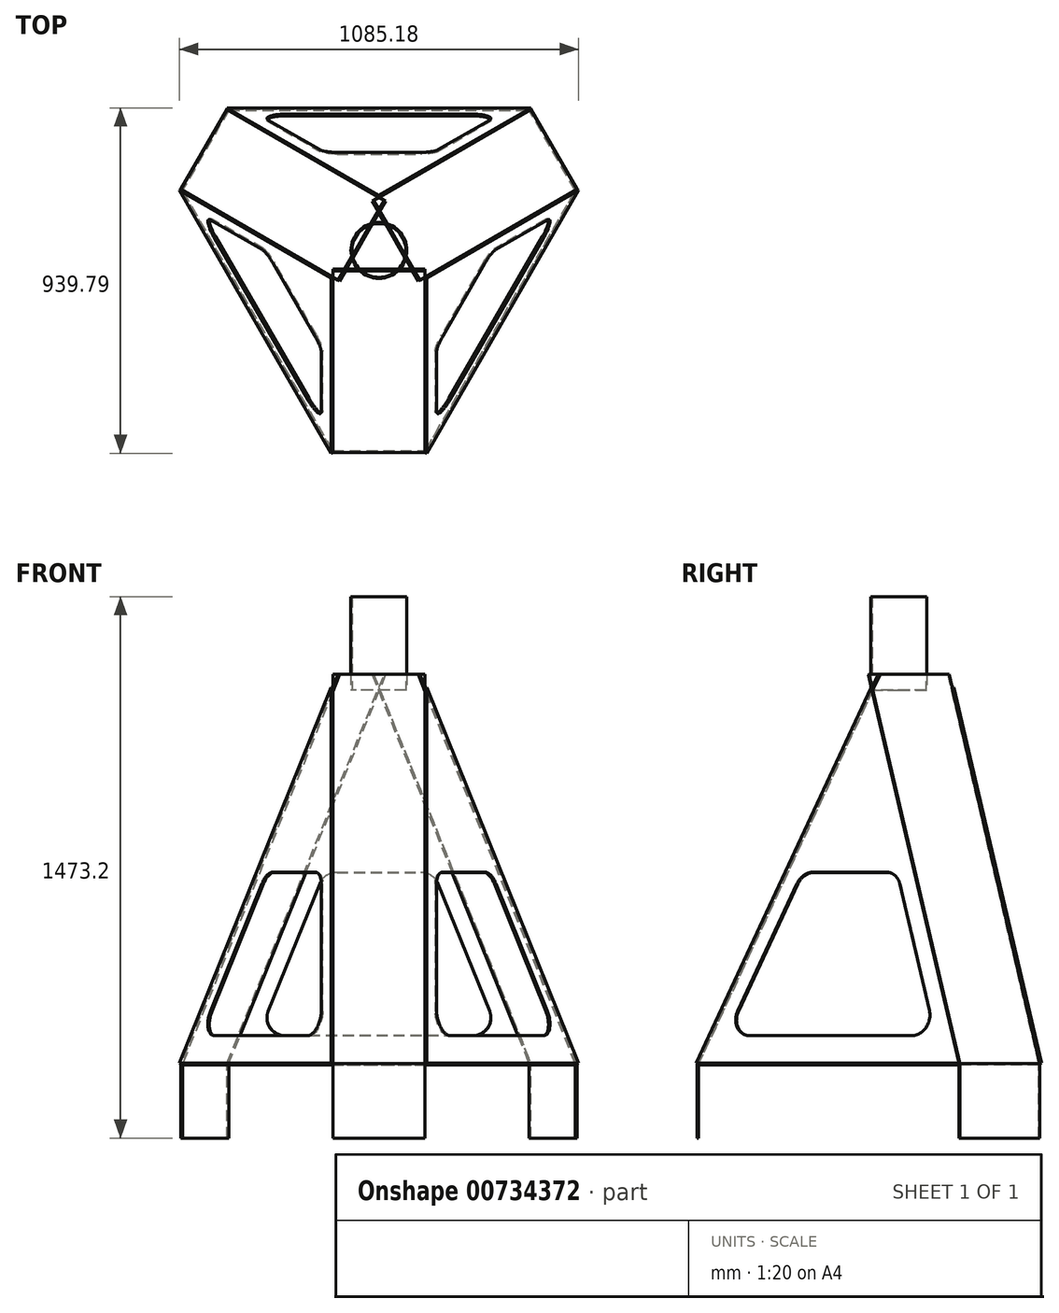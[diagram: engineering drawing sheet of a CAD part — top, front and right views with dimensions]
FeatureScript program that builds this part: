
annotation { "Feature Type Name" : "Feature", "Feature Type Description" : "" }
export const myFeature = defineFeature(function(context is Context, id is Id, definition is map)
    precondition{}
    {
        {
            var Q0;
            Q0=qCreatedBy(makeId("Top.planeOp"),FACE);
            var sketch = newSketch(context, id + "F0", { "sketchPlane" : qUnion([Q0])});
            skCircle(sketch, "E0", {"center": v(0, 0) * mm, "radius": 558.8 * mm});
            skLineSegment(sketch, "E1", {"start": v(0, 0) * mm, "end": v(0, -189.05) * mm});
            skLineSegment(sketch, "E2", {"start": v(-125.57, -544.5) * mm, "end": v(-534.34, 163.5) * mm});
            skLineSegment(sketch, "E3.1.0", {"start": v(534.34, 163.5) * mm, "end": v(125.57, -544.5) * mm});
            skLineSegment(sketch, "E3.2.0", {"start": v(-408.77, 381) * mm, "end": v(408.77, 381) * mm});
            skLineSegment(sketch, "E4", {"start": v(-125.57, -544.5) * mm, "end": v(125.57, -544.5) * mm});
            skLineSegment(sketch, "E5", {"start": v(-408.77, 381) * mm, "end": v(-534.34, 163.5) * mm});
            skLineSegment(sketch, "E6", {"start": v(408.77, 381) * mm, "end": v(534.34, 163.5) * mm});
            skSolve(sketch);
        }
        {
            var Q0;
            {var subQ0=sQuery(id+"F0.wireOp",EDGE,"E2");Q0=makeQuery(id+"F0.imprint","IMPRINT",FACE,{"disambiguationData":[TD([[makeQuery(id+"F0.imprint","IMPRINT",EDGE,{"derivedFrom":subQ0}),-1.0]])]});}
            extrude(context, id + "F1", {"entities" : qUnion([Q0]), "depth" : 4.83 * mm, "offsetDistance" : 25.4 * mm});
        }
        {
            var Q0;
            Q0=makeQuery(id+"F1.opExtrude","CAP_FACE",FACE,{"disambiguationData":[OSD([sQuery(id+"F0.wireOp",EDGE,"E2"),sQuery(id+"F0.wireOp",EDGE,"E3.1.0"),sQuery(id+"F0.wireOp",EDGE,"E3.2.0"),sQuery(id+"F0.wireOp",EDGE,"E4"),sQuery(id+"F0.wireOp",EDGE,"E5"),sQuery(id+"F0.wireOp",EDGE,"E6")])],"isStart":false});
            var sketch = newSketch(context, id + "F2", { "sketchPlane" : qUnion([Q0])});
            skLineSegment(sketch, "E7.bottom", {"start": v(-125.57, -544.5) * mm, "end": v(125.57, -544.5) * mm});
            skLineSegment(sketch, "E7.top", {"start": v(-125.57, -549.33) * mm, "end": v(125.57, -549.33) * mm});
            skLineSegment(sketch, "E7.left", {"start": v(-125.57, -544.5) * mm, "end": v(-125.57, -549.33) * mm});
            skLineSegment(sketch, "E7.right", {"start": v(125.57, -544.5) * mm, "end": v(125.57, -549.33) * mm});
            skSolve(sketch);
        }
        {
            var Q0;
            Q0 = qSketchRegion(id + "F2", true);
            extrude(context, id + "F3", {"entities" : qUnion([Q0]), "oppositeDirection" : true, "depth" : 203.2 * mm, "offsetDistance" : 25.4 * mm});
        }
        {
            var Q0;
            Q0=makeQuery(id+"F3.opExtrude","SWEPT_BODY",BODY,{"disambiguationData":[OSD([sQuery(id+"F2.wireOp",EDGE,"E7.bottom"),sQuery(id+"F2.wireOp",EDGE,"E7.top"),sQuery(id+"F2.wireOp",EDGE,"E7.left"),sQuery(id+"F2.wireOp",EDGE,"E7.right")])]});
            var Q1;
            Q1=sQuery(id+"F0.wireOp",EDGE,"E0");
            circularPattern(context, id + "F4", {"entities" : qUnion([Q0]), "axis" : qUnion([Q1]), "angle" : 360 * degree, "instanceCount" : 3, "equalSpace" : true});
        }
        {
            var Q0;
            Q0=makeQuery(id+"F1.opExtrude","CAP_FACE",FACE,{"disambiguationData":[OSD([sQuery(id+"F0.wireOp",EDGE,"E2"),sQuery(id+"F0.wireOp",EDGE,"E3.1.0"),sQuery(id+"F0.wireOp",EDGE,"E3.2.0"),sQuery(id+"F0.wireOp",EDGE,"E4"),sQuery(id+"F0.wireOp",EDGE,"E5"),sQuery(id+"F0.wireOp",EDGE,"E6")])],"isStart":false});
            cPlane(context, id + "F5", {"entities" : qUnion([Q0]), "cplaneType" : CPlaneType.OFFSET, "offset" : 1016 * mm, "width" : 152.4 * mm, "height" : 152.4 * mm});
        }
        {
            var Q0;
            Q0=qCreatedBy(id+"F5.planeOp",FACE);
            var sketch = newSketch(context, id + "F6", { "sketchPlane" : qUnion([Q0])});
            skPoint(sketch, "E8.middle", {"position": v(0, 0) * mm});
            skCircle(sketch, "E9", {"center": v(0, 0) * mm, "radius": 76.2 * mm});
            skCircle(sketch, "E10", {"center": v(0, 0) * mm, "radius": 73.15 * mm});
            skSolve(sketch);
        }
        {
            var Q0;
            Q0 = qSketchRegion(id + "F6", true);
            extrude(context, id + "F7", {"entities" : qUnion([Q0]), "depth" : 254 * mm, "offsetDistance" : 25.4 * mm});
        }
        {
            var Q0;
            Q0=makeQuery(id+"F4.opPattern","COPY",EDGE,{"derivedFrom":makeQuery(id+"F3.opExtrude","CAP_EDGE",EDGE,{"disambiguationData":[OSD([sQuery(id+"F2.wireOp",EDGE,"E7.top")])],"isStart":true}),"instanceName":"1"});
            cPlane(context, id + "F8", {"entities" : qUnion([Q0]), "cplaneType" : CPlaneType.LINE_ANGLE, "offset" : 25.4 * mm, "angle" : 65 * degree, "width" : 152.4 * mm, "height" : 152.4 * mm});
        }
        {
            var Q0;
            Q0=qCreatedBy(id+"F8.planeOp",FACE);
            var sketch = newSketch(context, id + "F9", { "sketchPlane" : qUnion([Q0])});
            skLineSegment(sketch, "E11.0", {"start": v(-68, -251.06) * mm, "end": v(175.98, -191.53) * mm});
            skLineSegment(sketch, "E12", {"start": v(-68, -251.06) * mm, "end": v(-344.96, 884.04) * mm});
            skLineSegment(sketch, "E13", {"start": v(-344.96, 884.04) * mm, "end": v(-100.98, 943.57) * mm});
            skLineSegment(sketch, "E14", {"start": v(-100.98, 943.57) * mm, "end": v(175.98, -191.53) * mm});
            skSolve(sketch);
        }
        {
            var Q0;
            Q0=makeQuery(id+"F9.imprint","IMPRINT",FACE,{"disambiguationData":[TD([[makeQuery(id+"F9.imprint","IMPRINT",EDGE,{"derivedFrom":sQuery(id+"F9.wireOp",EDGE,"E11.0")}),1.0]])]});
            extrude(context, id + "F10", {"entities" : qUnion([Q0]), "oppositeDirection" : true, "depth" : 4.83 * mm, "offsetDistance" : 25.4 * mm});
        }
        {
            var Q0;
            Q0=makeQuery(id+"F10.opExtrude","SWEPT_BODY",BODY,{"disambiguationData":[OSD([sQuery(id+"F9.wireOp",EDGE,"E11.0"),sQuery(id+"F9.wireOp",EDGE,"E12"),sQuery(id+"F9.wireOp",EDGE,"E13"),sQuery(id+"F9.wireOp",EDGE,"E14")])]});
            var Q1;
            Q1=sQuery(id+"F0.wireOp",EDGE,"E0");
            circularPattern(context, id + "F11", {"entities" : qUnion([Q0]), "axis" : qUnion([Q1]), "angle" : 360 * degree, "instanceCount" : 3, "equalSpace" : true});
        }
        {
            var Q0;
            Q0=makeQuery(id+"F4.opPattern","COPY",VERTEX,{"derivedFrom":makeQuery(id+"F3.opExtrude","CAP_VERTEX",VERTEX,{"disambiguationData":[OSD([sQuery(id+"F2.wireOp",EDGE,"E7.top"),sQuery(id+"F2.wireOp",EDGE,"E7.right")])],"isStart":true}),"instanceName":"1"});
            var Q1;
            Q1=makeQuery(id+"F4.opPattern","COPY",VERTEX,{"derivedFrom":makeQuery(id+"F3.opExtrude","CAP_VERTEX",VERTEX,{"disambiguationData":[OSD([sQuery(id+"F2.wireOp",EDGE,"E7.top"),sQuery(id+"F2.wireOp",EDGE,"E7.left")])],"isStart":true}),"instanceName":"2"});
            var Q2;
            Q2=makeQuery(id+"F11.opPattern","COPY",VERTEX,{"derivedFrom":makeQuery(id+"F10.opExtrude","CAP_VERTEX",VERTEX,{"disambiguationData":[OSD([sQuery(id+"F9.wireOp",EDGE,"E12"),sQuery(id+"F9.wireOp",EDGE,"E13")])],"isStart":true}),"instanceName":"1"});
            cPlane(context, id + "F12", {"entities" : qUnion([Q0, Q1, Q2]), "cplaneType" : CPlaneType.THREE_POINT, "offset" : 25.4 * mm, "width" : 152.4 * mm, "height" : 152.4 * mm});
        }
        {
            var Q0;
            Q0=qCreatedBy(id+"F12.planeOp",FACE);
            var sketch = newSketch(context, id + "F13", { "sketchPlane" : qUnion([Q0])});
            skLineSegment(sketch, "E15.0", {"start": v(0, 967.65) * mm, "end": v(412.95, -82.36) * mm});
            skLineSegment(sketch, "E16.0", {"start": v(-412.95, -82.36) * mm, "end": v(0, 967.65) * mm});
            skLineSegment(sketch, "E17", {"start": v(412.95, -82.36) * mm, "end": v(-412.95, -82.36) * mm});
            skPoint(sketch, "E18.orphan", {"position": v(-14.68, 1004.97) * mm});
            skPoint(sketch, "E19.orphan", {"position": v(14.68, 1004.97) * mm});
            skSolve(sketch);
        }
        {
            var Q0;
            Q0 = qSketchRegion(id + "F13", true);
            extrude(context, id + "F14", {"entities" : qUnion([Q0]), "oppositeDirection" : true, "depth" : 4.83 * mm, "offsetDistance" : 25.4 * mm});
        }
        {
            var Q0;
            Q0=makeQuery(id+"F14.opExtrude","CAP_FACE",FACE,{"disambiguationData":[OSD([sQuery(id+"F13.wireOp",EDGE,"E15.0"),sQuery(id+"F13.wireOp",EDGE,"E16.0"),sQuery(id+"F13.wireOp",EDGE,"E17")])],"isStart":false});
            var sketch = newSketch(context, id + "F15", { "sketchPlane" : qUnion([Q0])});
            skLineSegment(sketch, "E20", {"start": v(-253.83, -6.16) * mm, "end": v(253.83, -6.16) * mm});
            skLineSegment(sketch, "E21", {"start": v(301.1, 63.23) * mm, "end": v(161.25, 418.83) * mm});
            skLineSegment(sketch, "E22", {"start": v(113.98, 451.04) * mm, "end": v(-113.98, 451.04) * mm});
            skLineSegment(sketch, "E23", {"start": v(-161.25, 418.83) * mm, "end": v(-301.1, 63.23) * mm});
            skPoint(sketch, "E24.visualSharp", {"position": v(-148.59, 451.04) * mm});
            skArc(sketch, "E24.filletArc", {"start": v(-113.98, 451.04) * mm, "mid": v(-142.58, 442.22) * mm, "end": v(-161.25, 418.83) * mm});
            skPoint(sketch, "E25.visualSharp", {"position": v(148.59, 451.04) * mm});
            skArc(sketch, "E25.filletArc", {"start": v(161.25, 418.83) * mm, "mid": v(142.58, 442.22) * mm, "end": v(113.98, 451.04) * mm});
            skPoint(sketch, "E26.visualSharp", {"position": v(328.4, -6.16) * mm});
            skArc(sketch, "E26.filletArc", {"start": v(253.83, -6.16) * mm, "mid": v(295.81, 16.04) * mm, "end": v(301.1, 63.23) * mm});
            skPoint(sketch, "E27.visualSharp", {"position": v(-328.4, -6.16) * mm});
            skArc(sketch, "E27.filletArc", {"start": v(-301.1, 63.23) * mm, "mid": v(-295.81, 16.04) * mm, "end": v(-253.83, -6.16) * mm});
            skSolve(sketch);
        }
        {
            var Q0;
            Q0 = qSketchRegion(id + "F15", true);
            var Q1;
            Q1=makeQuery(id+"F14.opExtrude","CAP_FACE",FACE,{"disambiguationData":[OSD([sQuery(id+"F13.wireOp",EDGE,"E15.0"),sQuery(id+"F13.wireOp",EDGE,"E16.0"),sQuery(id+"F13.wireOp",EDGE,"E17")])],"isStart":true});
            extrude(context, id + "F16", {"entities" : qUnion([Q0]), "operationType" : NewBodyOperationType.REMOVE, "endBound" : BoundingType.UP_TO_SURFACE, "oppositeDirection" : true, "depth" : 25.4 * mm, "endBoundEntityFace" : qUnion([Q1]), "offsetDistance" : 25.4 * mm});
        }
        {
            var Q0;
            Q0=makeQuery(id+"F14.opExtrude","SWEPT_BODY",BODY,{"disambiguationData":[OSD([sQuery(id+"F13.wireOp",EDGE,"E15.0"),sQuery(id+"F13.wireOp",EDGE,"E16.0"),sQuery(id+"F13.wireOp",EDGE,"E17")])]});
            var Q1;
            Q1=sQuery(id+"F0.wireOp",EDGE,"E0");
            circularPattern(context, id + "F17", {"entities" : qUnion([Q0]), "axis" : qUnion([Q1]), "angle" : 360 * degree, "instanceCount" : 3, "equalSpace" : true});
        }
    });
